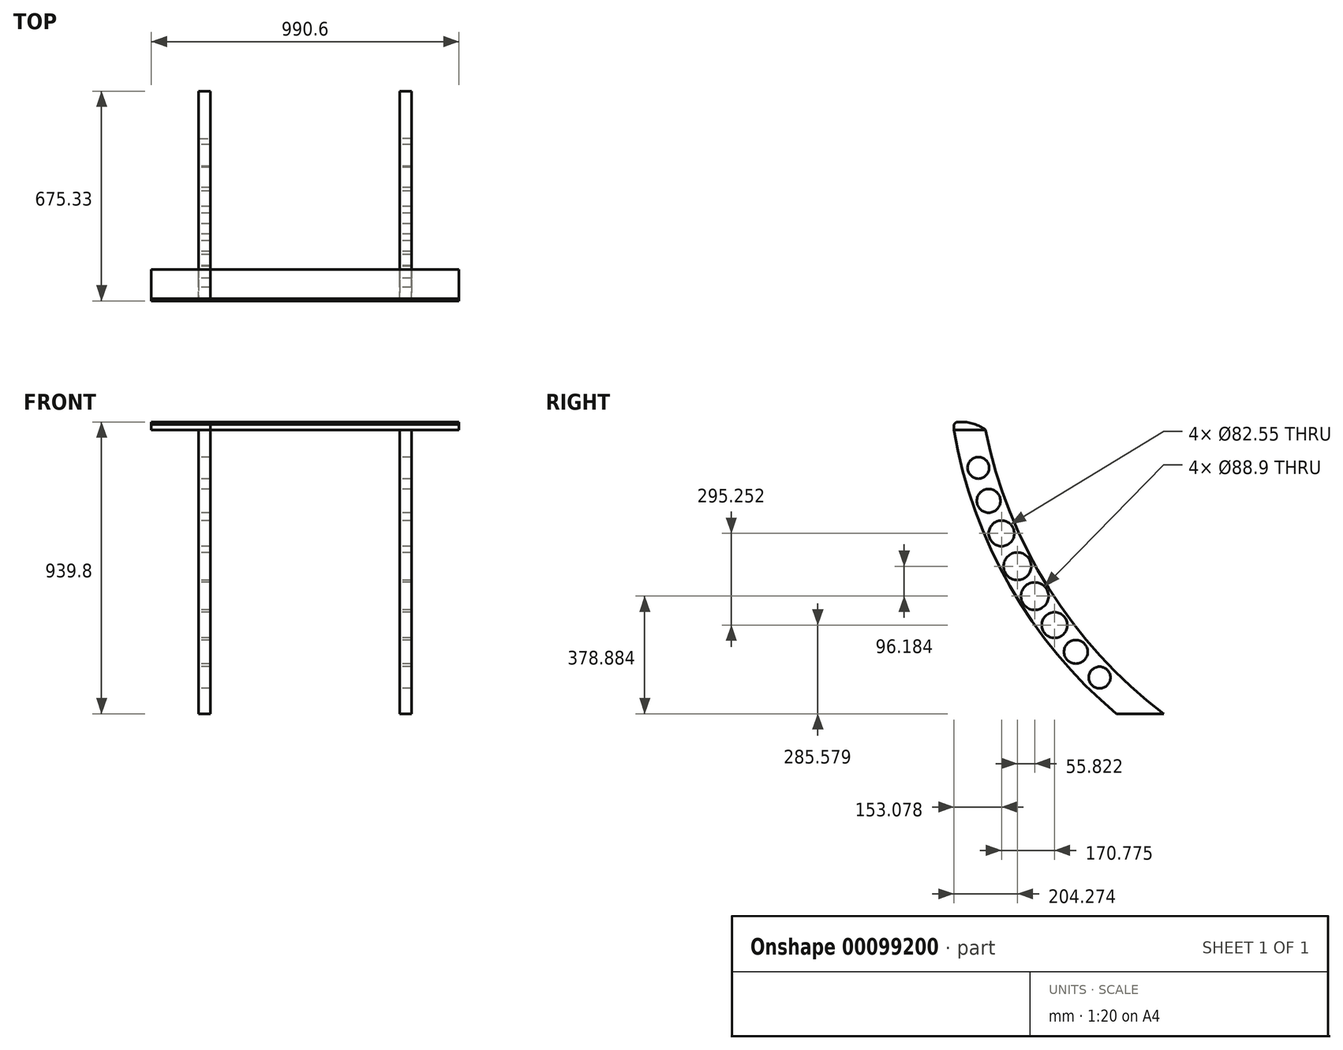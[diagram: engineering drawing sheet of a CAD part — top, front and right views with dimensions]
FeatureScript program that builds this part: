
annotation { "Feature Type Name" : "Feature", "Feature Type Description" : "" }
export const myFeature = defineFeature(function(context is Context, id is Id, definition is map)
    precondition{}
    {
        {
            var Q0;
            Q0=qCreatedBy(makeId("Right.planeOp"),FACE);
            var sketch = newSketch(context, id + "F0", { "sketchPlane" : qUnion([Q0])});
            skLineSegment(sketch, "E0", {"start": v(0, 0) * mm, "end": v(-152.4, 0) * mm});
            skArc(sketch, "E1", {"start": v(-675.33, 914.4) * mm, "mid": v(-495.38, 410.58) * mm, "end": v(-152.4, 0) * mm});
            skArc(sketch, "E2", {"start": v(-573.73, 914.4) * mm, "mid": v(-370.54, 404.7) * mm, "end": v(0, 0) * mm});
            skLineSegment(sketch, "E3", {"start": v(-573.73, 914.4) * mm, "end": v(-675.33, 914.4) * mm});
            skSolve(sketch);
        }
        {
            var Q0;
            Q0=makeQuery(id+"F0.imprint","IMPRINT",FACE,{"disambiguationData":[TD([[makeQuery(id+"F0.imprint","IMPRINT",EDGE,{"derivedFrom":sQuery(id+"F0.wireOp",EDGE,"E0")}),-1.0]])]});
            extrude(context, id + "F1", {"entities" : qUnion([Q0]), "depth" : 38.1 * mm});
        }
        {
            var Q0;
            Q0=makeQuery(id+"F1.opExtrude","SWEPT_FACE",FACE,{"disambiguationData":[OSD([sQuery(id+"F0.wireOp",EDGE,"E3")])]});
            var sketch = newSketch(context, id + "F2", { "sketchPlane" : qUnion([Q0])});
            skLineSegment(sketch, "E4", {"start": v(0, -573.73) * mm, "end": v(-609.6, -573.73) * mm});
            skLineSegment(sketch, "E5", {"start": v(0, -675.33) * mm, "end": v(-609.6, -675.33) * mm});
            skLineSegment(sketch, "E6", {"start": v(-609.6, -675.33) * mm, "end": v(-609.6, -573.73) * mm});
            skLineSegment(sketch, "E7", {"start": v(0, -573.73) * mm, "end": v(190.5, -573.73) * mm});
            skLineSegment(sketch, "E8", {"start": v(190.5, -573.73) * mm, "end": v(190.5, -675.33) * mm});
            skLineSegment(sketch, "E9", {"start": v(190.5, -675.33) * mm, "end": v(0, -675.33) * mm});
            skSolve(sketch);
        }
        {
            var Q0;
            Q0=makeQuery(id+"F2.imprint","IMPRINT",FACE,{"disambiguationData":[TD([[makeQuery(id+"F2.imprint","IMPRINT",EDGE,{"derivedFrom":sQuery(id+"F2.wireOp",EDGE,"E4")}),1.0]])]});
            var Q1;
            {var subQ2=sQuery(id+"F2.wireOp",EDGE,"E8");Q1=makeQuery(id+"F2.imprint","IMPRINT",FACE,{"disambiguationData":[TD([[makeQuery(id+"F2.imprint","IMPRINT",EDGE,{"derivedFrom":subQ2}),-1.0]])]});}
            var Q2;
            {var subQ1=sQuery(id+"F0.wireOp",EDGE,"E3");var subQ2=makeQuery(id+"F1.opExtrude","CAP_EDGE",EDGE,{"disambiguationData":[OSD([subQ1])],"isStart":true});Q2=makeQuery(id+"F2.imprint","IMPRINT",FACE,{"disambiguationData":[TD([[makeQuery(id+"F2.imprint","IMPRINT",EDGE,{"derivedFrom":subQ2}),1.0]])]});}
            extrude(context, id + "F3", {"entities" : qUnion([Q0, Q1, Q2]), "operationType" : NewBodyOperationType.ADD, "depth" : 25.4 * mm});
        }
        {
            var Q0;
            Q0=makeQuery(id+"F3.opExtrude","SWEPT_FACE",FACE,{"disambiguationData":[OSD([sQuery(id+"F2.wireOp",EDGE,"E6")])]});
            var sketch = newSketch(context, id + "F4", { "sketchPlane" : qUnion([Q0])});
            skLineSegment(sketch, "E10", {"start": v(573.73, 914.4) * mm, "end": v(675.33, 914.4) * mm});
            skArc(sketch, "E11", {"start": v(0, 0) * mm, "mid": v(370.54, 404.7) * mm, "end": v(573.73, 914.4) * mm});
            skArc(sketch, "E12", {"start": v(152.4, 0) * mm, "mid": v(495.38, 410.58) * mm, "end": v(675.33, 914.4) * mm});
            skLineSegment(sketch, "E13", {"start": v(0, 0) * mm, "end": v(152.4, 0) * mm});
            skSolve(sketch);
        }
        {
            var Q0;
            Q0=makeQuery(id+"F4.imprint","IMPRINT",FACE,{"disambiguationData":[TD([[makeQuery(id+"F4.imprint","IMPRINT",EDGE,{"derivedFrom":sQuery(id+"F4.wireOp",EDGE,"E10")}),1.0]])]});
            extrude(context, id + "F5", {"entities" : qUnion([Q0]), "depth" : 38.1 * mm});
        }
        {
            var Q0;
            Q0=makeQuery(id+"F5.opExtrude","SWEPT_FACE",FACE,{"disambiguationData":[OSD([sQuery(id+"F4.wireOp",EDGE,"E10")])]});
            var sketch = newSketch(context, id + "F6", { "sketchPlane" : qUnion([Q0])});
            skLineSegment(sketch, "E14", {"start": v(-609.6, -573.73) * mm, "end": v(-800.1, -573.73) * mm});
            skLineSegment(sketch, "E15", {"start": v(-800.1, -573.73) * mm, "end": v(-800.1, -675.33) * mm});
            skLineSegment(sketch, "E16", {"start": v(-800.1, -675.33) * mm, "end": v(-609.6, -675.33) * mm});
            skSolve(sketch);
        }
        {
            var Q0;
            {var subQ2=sQuery(id+"F6.wireOp",EDGE,"E15");Q0=makeQuery(id+"F6.imprint","IMPRINT",FACE,{"disambiguationData":[TD([[makeQuery(id+"F6.imprint","IMPRINT",EDGE,{"derivedFrom":subQ2}),1.0]])]});}
            var Q1;
            {var subQ1=sQuery(id+"F4.wireOp",EDGE,"E10");var subQ2=makeQuery(id+"F5.opExtrude","CAP_EDGE",EDGE,{"disambiguationData":[OSD([subQ1])],"isStart":true});Q1=makeQuery(id+"F6.imprint","IMPRINT",FACE,{"disambiguationData":[TD([[makeQuery(id+"F6.imprint","IMPRINT",EDGE,{"derivedFrom":subQ2}),1.0]])]});}
            extrude(context, id + "F7", {"entities" : qUnion([Q0, Q1]), "depth" : 25.4 * mm});
        }
        {
            var Q0;
            Q0=makeQuery(id+"F7.opExtrude","CAP_EDGE",EDGE,{"disambiguationData":[OSD([sQuery(id+"F6.wireOp",EDGE,"E14")])],"isStart":false});
            var Q1;
            Q1=makeQuery(id+"F3.opExtrude","CAP_EDGE",EDGE,{"disambiguationData":[OSD([sQuery(id+"F2.wireOp",EDGE,"E4"),sQuery(id+"F2.wireOp",EDGE,"E7")])],"isStart":false});
            fillet(context, id + "F8", {"entities" : qUnion([Q0, Q1]), "radius" : 127 * mm, "tangentPropagation" : true, "allowEdgeOverflow" : false});
        }
        {
            var Q0;
            Q0=makeQuery(id+"F7.opExtrude","CAP_EDGE",EDGE,{"disambiguationData":[OSD([sQuery(id+"F6.wireOp",EDGE,"E16")])],"isStart":false});
            var Q1;
            Q1=makeQuery(id+"F3.opExtrude","CAP_EDGE",EDGE,{"disambiguationData":[OSD([sQuery(id+"F2.wireOp",EDGE,"E5"),sQuery(id+"F2.wireOp",EDGE,"E9")])],"isStart":false});
            chamfer(context, id + "F9", {"entities" : qUnion([Q0, Q1]), "width" : 7.62 * mm, "tangentPropagation" : true});
        }
        {
            var Q0;
            Q0=makeQuery(id+"F5.opExtrude","CAP_FACE",FACE,{"disambiguationData":[OSD([sQuery(id+"F4.wireOp",EDGE,"E10"),sQuery(id+"F4.wireOp",EDGE,"E11"),sQuery(id+"F4.wireOp",EDGE,"E12"),sQuery(id+"F4.wireOp",EDGE,"E13")])],"isStart":false});
            var sketch = newSketch(context, id + "F10", { "sketchPlane" : qUnion([Q0])});
            skArc(sketch, "E17", {"start": v(76.2, 0) * mm, "mid": v(432.94, 407.68) * mm, "end": v(624.53, 914.4) * mm});
            skCircle(sketch, "E18", {"center": v(596.67, 792.07) * mm, "radius": 34.93 * mm});
            skCircle(sketch, "E19", {"center": v(522.25, 580.83) * mm, "radius": 41.28 * mm});
            skCircle(sketch, "E20", {"center": v(563.59, 685.77) * mm, "radius": 38.1 * mm});
            skCircle(sketch, "E21", {"center": v(471.06, 475.07) * mm, "radius": 44.45 * mm});
            skCircle(sketch, "E22", {"center": v(415.23, 378.88) * mm, "radius": 44.45 * mm});
            skCircle(sketch, "E23", {"center": v(351.48, 285.58) * mm, "radius": 41.28 * mm});
            skCircle(sketch, "E24", {"center": v(282.83, 199.4) * mm, "radius": 38.1 * mm});
            skCircle(sketch, "E25", {"center": v(206.42, 116.69) * mm, "radius": 34.93 * mm});
            skSolve(sketch);
        }
        {
            var Q0;
            {var subQ0=sQuery(id+"F10.wireOp",EDGE,"E18");var subQ1=sQuery(id+"F10.wireOp",EDGE,"E17");var subQ2=makeQuery(id+"F10.imprint","INTERSECT",VERTEX,{"disambiguationData":[OD(0.0)],"derivedFrom":[subQ1,subQ0]});Q0=makeQuery(id+"F10.imprint","IMPRINT",FACE,{"disambiguationData":[TD([[makeQuery(id+"F10.imprint","IMPRINT",EDGE,{"disambiguationData":[TD([[subQ2,-1.0]])],"derivedFrom":subQ1}),-1.0]])]});}
            var Q1;
            {var subQ0=sQuery(id+"F10.wireOp",EDGE,"E18");var subQ1=sQuery(id+"F10.wireOp",EDGE,"E17");var subQ2=makeQuery(id+"F10.imprint","INTERSECT",VERTEX,{"disambiguationData":[OD(0.0)],"derivedFrom":[subQ1,subQ0]});Q1=makeQuery(id+"F10.imprint","IMPRINT",FACE,{"disambiguationData":[TD([[makeQuery(id+"F10.imprint","IMPRINT",EDGE,{"disambiguationData":[TD([[subQ2,-1.0]])],"derivedFrom":subQ1}),1.0]])]});}
            var Q2;
            {var subQ0=sQuery(id+"F10.wireOp",EDGE,"E20");var subQ1=sQuery(id+"F10.wireOp",EDGE,"E17");var subQ2=makeQuery(id+"F10.imprint","INTERSECT",VERTEX,{"disambiguationData":[OD(0.0)],"derivedFrom":[subQ1,subQ0]});Q2=makeQuery(id+"F10.imprint","IMPRINT",FACE,{"disambiguationData":[TD([[makeQuery(id+"F10.imprint","IMPRINT",EDGE,{"disambiguationData":[TD([[subQ2,-1.0]])],"derivedFrom":subQ1}),1.0]])]});}
            var Q3;
            {var subQ0=sQuery(id+"F10.wireOp",EDGE,"E20");var subQ1=sQuery(id+"F10.wireOp",EDGE,"E17");var subQ2=makeQuery(id+"F10.imprint","INTERSECT",VERTEX,{"disambiguationData":[OD(0.0)],"derivedFrom":[subQ1,subQ0]});Q3=makeQuery(id+"F10.imprint","IMPRINT",FACE,{"disambiguationData":[TD([[makeQuery(id+"F10.imprint","IMPRINT",EDGE,{"disambiguationData":[TD([[subQ2,-1.0]])],"derivedFrom":subQ1}),-1.0]])]});}
            var Q4;
            {var subQ0=sQuery(id+"F10.wireOp",EDGE,"E19");var subQ1=sQuery(id+"F10.wireOp",EDGE,"E17");var subQ2=makeQuery(id+"F10.imprint","INTERSECT",VERTEX,{"disambiguationData":[OD(0.0)],"derivedFrom":[subQ1,subQ0]});Q4=makeQuery(id+"F10.imprint","IMPRINT",FACE,{"disambiguationData":[TD([[makeQuery(id+"F10.imprint","IMPRINT",EDGE,{"disambiguationData":[TD([[subQ2,-1.0]])],"derivedFrom":subQ1}),-1.0]])]});}
            var Q5;
            {var subQ0=sQuery(id+"F10.wireOp",EDGE,"E19");var subQ1=sQuery(id+"F10.wireOp",EDGE,"E17");var subQ2=makeQuery(id+"F10.imprint","INTERSECT",VERTEX,{"disambiguationData":[OD(0.0)],"derivedFrom":[subQ1,subQ0]});Q5=makeQuery(id+"F10.imprint","IMPRINT",FACE,{"disambiguationData":[TD([[makeQuery(id+"F10.imprint","IMPRINT",EDGE,{"disambiguationData":[TD([[subQ2,-1.0]])],"derivedFrom":subQ1}),1.0]])]});}
            var Q6;
            {var subQ0=sQuery(id+"F10.wireOp",EDGE,"E21");var subQ1=sQuery(id+"F10.wireOp",EDGE,"E17");var subQ2=makeQuery(id+"F10.imprint","INTERSECT",VERTEX,{"disambiguationData":[OD(0.0)],"derivedFrom":[subQ1,subQ0]});Q6=makeQuery(id+"F10.imprint","IMPRINT",FACE,{"disambiguationData":[TD([[makeQuery(id+"F10.imprint","IMPRINT",EDGE,{"disambiguationData":[TD([[subQ2,-1.0]])],"derivedFrom":subQ1}),-1.0]])]});}
            var Q7;
            {var subQ0=sQuery(id+"F10.wireOp",EDGE,"E21");var subQ1=sQuery(id+"F10.wireOp",EDGE,"E17");var subQ2=makeQuery(id+"F10.imprint","INTERSECT",VERTEX,{"disambiguationData":[OD(0.0)],"derivedFrom":[subQ1,subQ0]});Q7=makeQuery(id+"F10.imprint","IMPRINT",FACE,{"disambiguationData":[TD([[makeQuery(id+"F10.imprint","IMPRINT",EDGE,{"disambiguationData":[TD([[subQ2,-1.0]])],"derivedFrom":subQ1}),1.0]])]});}
            var Q8;
            {var subQ0=sQuery(id+"F10.wireOp",EDGE,"E22");var subQ1=sQuery(id+"F10.wireOp",EDGE,"E17");var subQ2=makeQuery(id+"F10.imprint","INTERSECT",VERTEX,{"disambiguationData":[OD(0.0)],"derivedFrom":[subQ1,subQ0]});Q8=makeQuery(id+"F10.imprint","IMPRINT",FACE,{"disambiguationData":[TD([[makeQuery(id+"F10.imprint","IMPRINT",EDGE,{"disambiguationData":[TD([[subQ2,-1.0]])],"derivedFrom":subQ1}),1.0]])]});}
            var Q9;
            {var subQ0=sQuery(id+"F10.wireOp",EDGE,"E22");var subQ1=sQuery(id+"F10.wireOp",EDGE,"E17");var subQ2=makeQuery(id+"F10.imprint","INTERSECT",VERTEX,{"disambiguationData":[OD(0.0)],"derivedFrom":[subQ1,subQ0]});Q9=makeQuery(id+"F10.imprint","IMPRINT",FACE,{"disambiguationData":[TD([[makeQuery(id+"F10.imprint","IMPRINT",EDGE,{"disambiguationData":[TD([[subQ2,-1.0]])],"derivedFrom":subQ1}),-1.0]])]});}
            var Q10;
            {var subQ0=sQuery(id+"F10.wireOp",EDGE,"E23");var subQ1=sQuery(id+"F10.wireOp",EDGE,"E17");var subQ2=makeQuery(id+"F10.imprint","INTERSECT",VERTEX,{"disambiguationData":[OD(0.0)],"derivedFrom":[subQ1,subQ0]});Q10=makeQuery(id+"F10.imprint","IMPRINT",FACE,{"disambiguationData":[TD([[makeQuery(id+"F10.imprint","IMPRINT",EDGE,{"disambiguationData":[TD([[subQ2,-1.0]])],"derivedFrom":subQ1}),-1.0]])]});}
            var Q11;
            {var subQ0=sQuery(id+"F10.wireOp",EDGE,"E24");var subQ1=sQuery(id+"F10.wireOp",EDGE,"E17");var subQ2=makeQuery(id+"F10.imprint","INTERSECT",VERTEX,{"disambiguationData":[OD(0.0)],"derivedFrom":[subQ1,subQ0]});Q11=makeQuery(id+"F10.imprint","IMPRINT",FACE,{"disambiguationData":[TD([[makeQuery(id+"F10.imprint","IMPRINT",EDGE,{"disambiguationData":[TD([[subQ2,-1.0]])],"derivedFrom":subQ1}),1.0]])]});}
            var Q12;
            {var subQ0=sQuery(id+"F10.wireOp",EDGE,"E24");var subQ1=sQuery(id+"F10.wireOp",EDGE,"E17");var subQ2=makeQuery(id+"F10.imprint","INTERSECT",VERTEX,{"disambiguationData":[OD(0.0)],"derivedFrom":[subQ1,subQ0]});Q12=makeQuery(id+"F10.imprint","IMPRINT",FACE,{"disambiguationData":[TD([[makeQuery(id+"F10.imprint","IMPRINT",EDGE,{"disambiguationData":[TD([[subQ2,-1.0]])],"derivedFrom":subQ1}),-1.0]])]});}
            var Q13;
            {var subQ0=sQuery(id+"F10.wireOp",EDGE,"E23");var subQ1=sQuery(id+"F10.wireOp",EDGE,"E17");var subQ2=makeQuery(id+"F10.imprint","INTERSECT",VERTEX,{"disambiguationData":[OD(0.0)],"derivedFrom":[subQ1,subQ0]});Q13=makeQuery(id+"F10.imprint","IMPRINT",FACE,{"disambiguationData":[TD([[makeQuery(id+"F10.imprint","IMPRINT",EDGE,{"disambiguationData":[TD([[subQ2,-1.0]])],"derivedFrom":subQ1}),1.0]])]});}
            var Q14;
            {var subQ0=sQuery(id+"F10.wireOp",EDGE,"E25");var subQ1=sQuery(id+"F10.wireOp",EDGE,"E17");var subQ2=makeQuery(id+"F10.imprint","INTERSECT",VERTEX,{"disambiguationData":[OD(0.0)],"derivedFrom":[subQ1,subQ0]});Q14=makeQuery(id+"F10.imprint","IMPRINT",FACE,{"disambiguationData":[TD([[makeQuery(id+"F10.imprint","IMPRINT",EDGE,{"disambiguationData":[TD([[subQ2,-1.0]])],"derivedFrom":subQ1}),1.0]])]});}
            var Q15;
            {var subQ0=sQuery(id+"F10.wireOp",EDGE,"E25");var subQ1=sQuery(id+"F10.wireOp",EDGE,"E17");var subQ2=makeQuery(id+"F10.imprint","INTERSECT",VERTEX,{"disambiguationData":[OD(0.0)],"derivedFrom":[subQ1,subQ0]});Q15=makeQuery(id+"F10.imprint","IMPRINT",FACE,{"disambiguationData":[TD([[makeQuery(id+"F10.imprint","IMPRINT",EDGE,{"disambiguationData":[TD([[subQ2,-1.0]])],"derivedFrom":subQ1}),-1.0]])]});}
            extrude(context, id + "F11", {"entities" : qUnion([Q0, Q1, Q2, Q3, Q4, Q5, Q6, Q7, Q8, Q9, Q10, Q11, Q12, Q13, Q14, Q15]), "operationType" : NewBodyOperationType.REMOVE, "oppositeDirection" : true, "depth" : 762 * mm});
        }
    });
